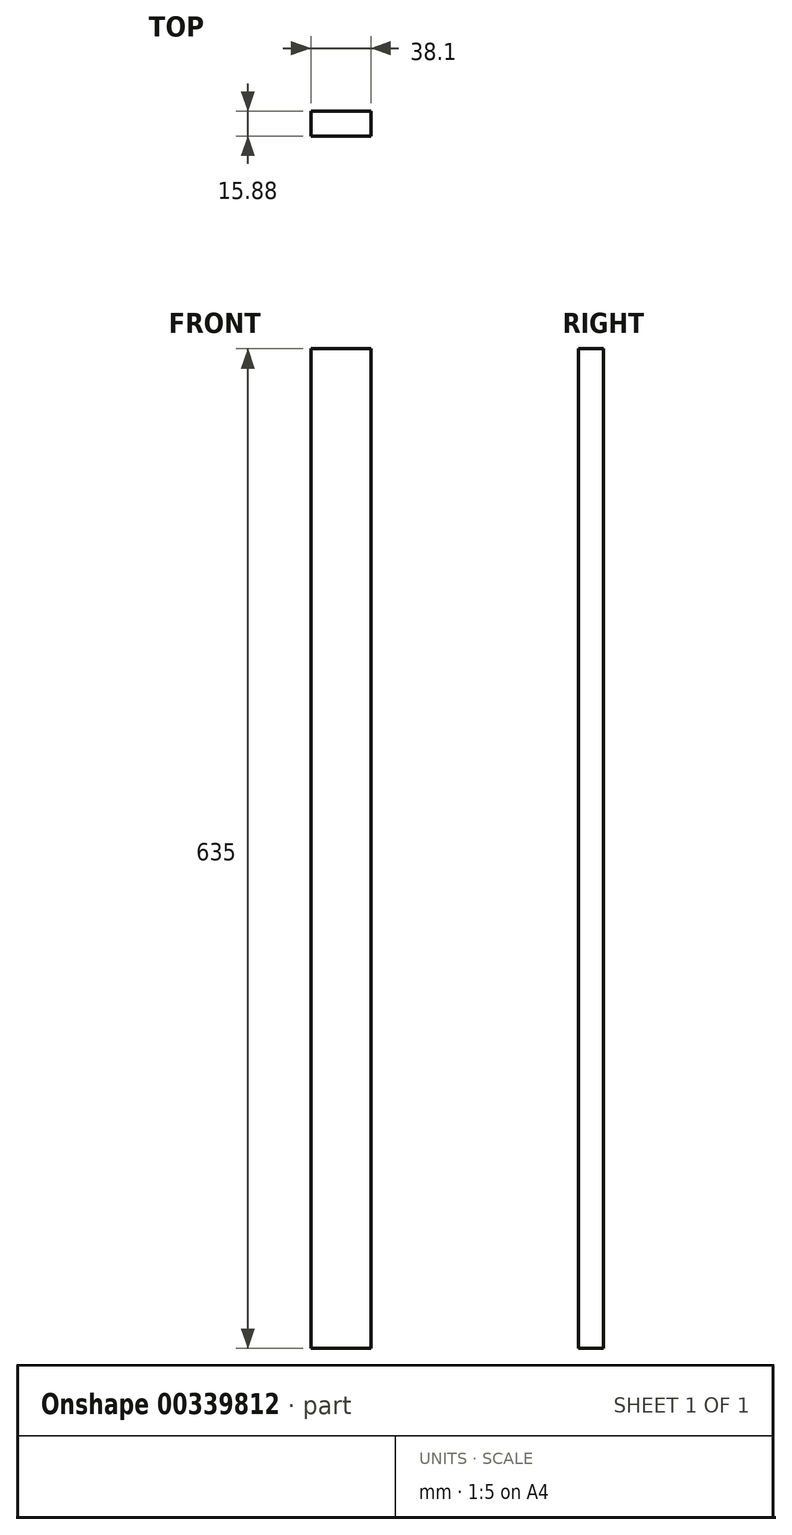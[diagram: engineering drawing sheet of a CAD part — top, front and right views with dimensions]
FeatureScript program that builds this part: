
annotation { "Feature Type Name" : "Feature", "Feature Type Description" : "" }
export const myFeature = defineFeature(function(context is Context, id is Id, definition is map)
    precondition{}
    {
        {
            var Q0;
            Q0=qCreatedBy(makeId("Front.planeOp"),FACE);
            var sketch = newSketch(context, id + "F0", { "sketchPlane" : qUnion([Q0])});
            skLineSegment(sketch, "E0.bottom", {"start": v(-40.34, 531.78) * mm, "end": v(-2.24, 531.78) * mm});
            skLineSegment(sketch, "E0.top", {"start": v(-40.34, -103.22) * mm, "end": v(-2.24, -103.22) * mm});
            skLineSegment(sketch, "E0.left", {"start": v(-40.34, 531.78) * mm, "end": v(-40.34, -103.22) * mm});
            skLineSegment(sketch, "E0.right", {"start": v(-2.24, 531.78) * mm, "end": v(-2.24, -103.22) * mm});
            skSolve(sketch);
        }
        {
            var Q0;
            Q0 = qSketchRegion(id + "F0", true);
            extrude(context, id + "F1", {"entities" : qUnion([Q0]), "oppositeDirection" : true, "depth" : 15.88 * mm});
        }
    });
